# Revit family: Resan Anti-Ligature Basin Central Tap Right Sensor Hole
name_source: partatom
category: Plumbing Fixtures
revit_build: Autodesk Revit 2017 (Build: 20160225_1515(x64)
units: mm (PartAtom-declared; Revit-internal decimal feet)

## family parameters
Cut with Voids When Loaded = No
Host = Face
Part Type = Normal
Room Calculation Point = No
Round Connector Dimension = Use Diameter
Shared = No

## types (1)
- Resan Anti-Ligature Basin Central Tap Right Sensor Hole
    326172 Light Touch Activation = No
    326173 Infra-red Activation = Yes
    Access Clearance Bottom = 0 mm  [stored 0 ft]
    Access Clearance Front = 0 mm  [stored 0 ft]
    Access Clearance Left = 0 mm  [stored 0 ft]
    Access Clearance Rear = 0 mm  [stored 0 ft]
    Access Clearance Right = 0 mm  [stored 0 ft]
    Access Clearance Top = 0 mm  [stored 0 ft]
    Anti-Vandal = Yes
    CE Approval = Yes
    Colour = White
    Coverage Area = 0.05m^3
    Default Elevation = 1219 mm
    Description = Basin
    Features = Anti-Vandal
    Finish = Polished Gloss
    Gross Weight = 21kg
    IP Rating = IP65
    Inlet Diameter = 15mm
    Installation Type = Wall
    Issue = 1
    Maintenance Instructions = Refer to instructions
    Mandatory Requirements = 326171 Tempomatic multifunction 8-way, 326174 Solenoid valve, 326175 & 326176 Colour coded markers
    Manufacturer = Thomas Dudley Ltd
    Manufacturer Country = United Kingdom
    Material = Polyester Resin
    Material Finish = Polished Gloss White
    Model = Resan Basin
    No. Of Poles = 0
    Outlet Diameter = 32mm
    Overall Height = 318 mm  [stored 1.04331 ft]
    Overall Length = 336 mm  [stored 1.10236 ft]
    Overall Width = 460 mm  [stored 1.50919 ft]
    Power Source = 230V Mains
    Product Code = PRESBA334847
    Product Instructions = http://www.thomasdudley.co.uk
    Product Literature = http://www.dudleyresan.co.uk
    Product Range = Resan
    Publish Date = 02/10/2019
    Reference Standard = BS EN 14688:2005 & BS EN 31:2009
    Servicing = Refer to instructions
    Shipping Weight = 23KG
    Spares = http://spares.thomasdudley.co.uk
    Type = Basin
    URL = www.thomasdudley.co.uk
    Voltage = 12V
    Warranty = 5 Years
    Warranty Type = Parts
    YouTube Link = https://youtu.be

note: [stored X ft] marks values corroborated as IEEE doubles in the binary element streams (Revit-internal decimal feet)

## geometry (parser evidence)
native form markers: Sweep x7
no freeform markers — native parametric forms only
